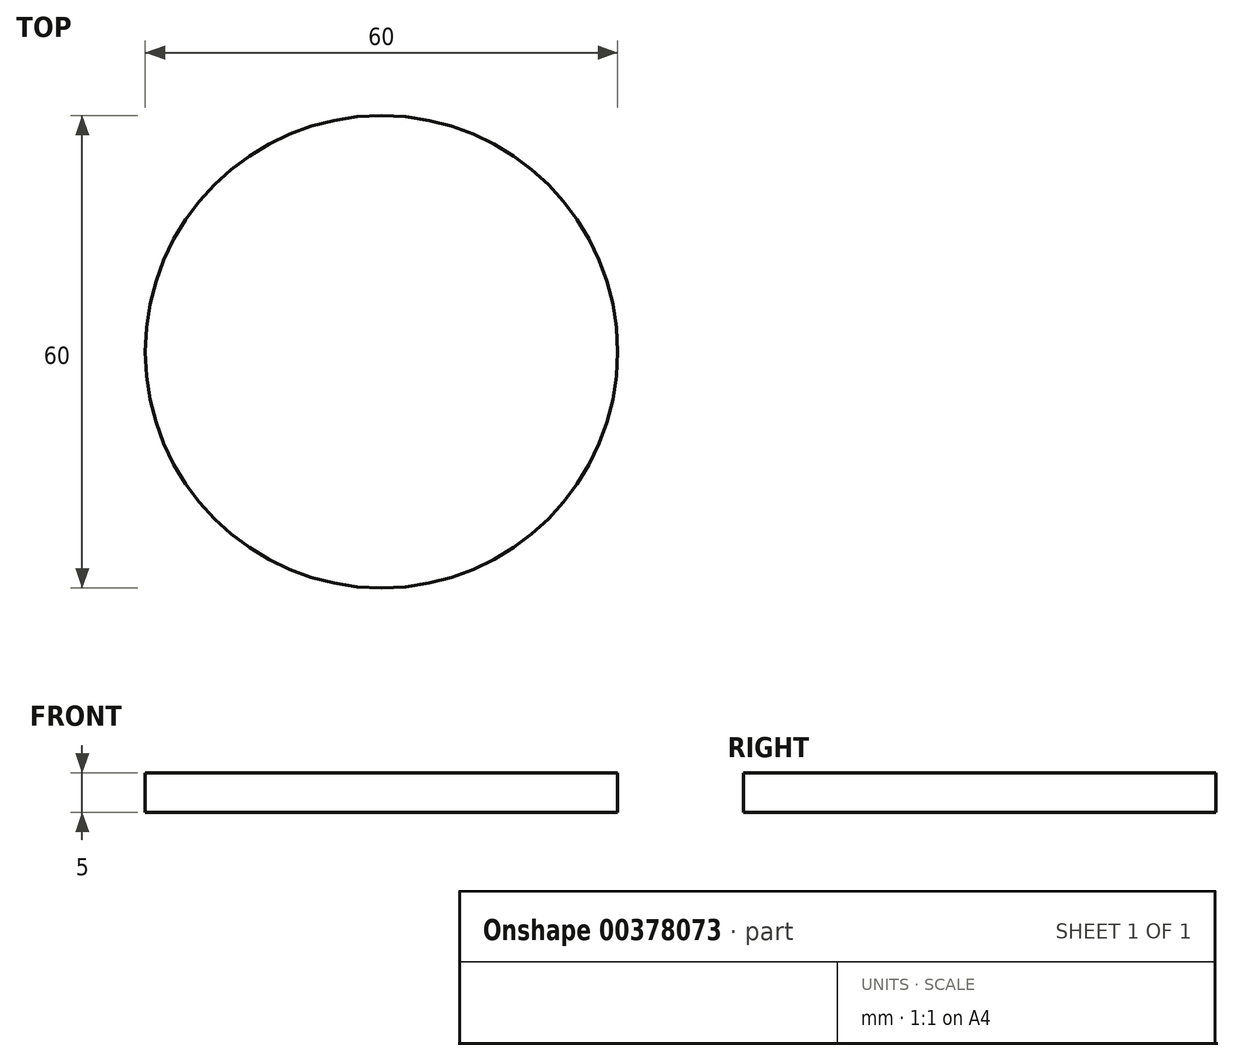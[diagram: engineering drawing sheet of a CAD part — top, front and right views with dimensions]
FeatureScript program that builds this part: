
annotation { "Feature Type Name" : "Feature", "Feature Type Description" : "" }
export const myFeature = defineFeature(function(context is Context, id is Id, definition is map)
    precondition{}
    {
        {
            var Q0;
            Q0=qCreatedBy(makeId("Front.planeOp"),FACE);
            var sketch = newSketch(context, id + "F0", { "sketchPlane" : qUnion([Q0])});
            skLineSegment(sketch, "E0.bottom", {"start": v(0, 5) * mm, "end": v(30, 5) * mm});
            skLineSegment(sketch, "E0.top", {"start": v(0, 0) * mm, "end": v(30, 0) * mm});
            skLineSegment(sketch, "E0.left", {"start": v(0, 5) * mm, "end": v(0, 0) * mm});
            skLineSegment(sketch, "E0.right", {"start": v(30, 5) * mm, "end": v(30, 0) * mm});
            skSolve(sketch);
        }
        {
            var Q0;
            Q0=makeQuery(id+"F0.imprint","IMPRINT",FACE,{"disambiguationData":[TD([[makeQuery(id+"F0.imprint","IMPRINT",EDGE,{"derivedFrom":sQuery(id+"F0.wireOp",EDGE,"E0.bottom")}),-1.0]])]});
            var Q1;
            Q1=sQuery(id+"F0.wireOp",EDGE,"E0.left");
            revolve(context, id + "F1", {"entities" : qUnion([Q0]), "axis" : qUnion([Q1]), "revolveType" : RevolveType.FULL});
        }
    });
